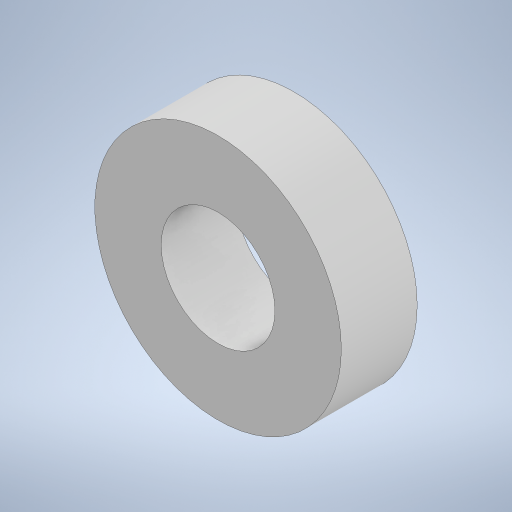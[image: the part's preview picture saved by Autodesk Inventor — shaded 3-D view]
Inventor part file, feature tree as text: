
AUTODESK INVENTOR PART (.ipt)
format: ipt  version: 2023 (Build 270158000, 158)  size: 214,016 bytes
history: native  units: in
note: dims shown in document units (in); Inventor stores cm internally (conversion verified against a paired STEP export)
features: extrude x1, sketch x1
ambient origin geometry x8: Origin, YZ Plane, XZ Plane, XY Plane, X Axis, Y Axis, Z Axis, Center Point
bodies: Solid1 (feature_tree)
feature tree (2):
  extrude  "Extrusion1"  Depth=0.5in
  sketch  "Sketch1"  dims[d0=0.75in d1=1.625in d2=0.5in d3=0.0in]
